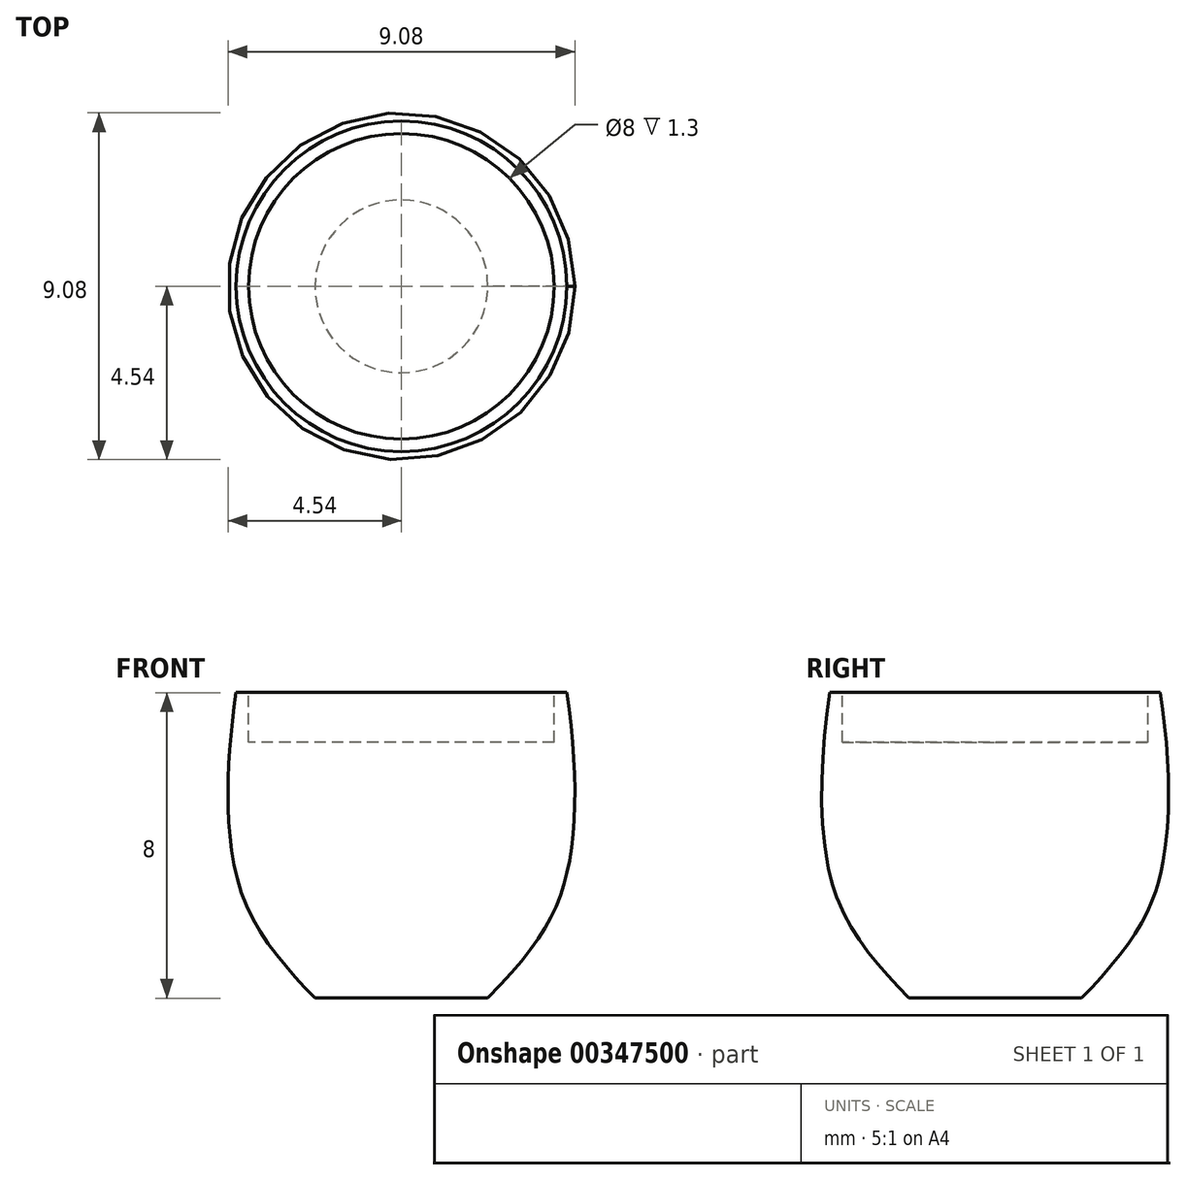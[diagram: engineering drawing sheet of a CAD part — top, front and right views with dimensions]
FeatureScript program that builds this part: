
annotation { "Feature Type Name" : "Feature", "Feature Type Description" : "" }
export const myFeature = defineFeature(function(context is Context, id is Id, definition is map)
    precondition{}
    {
        {
            var Q0;
            Q0=qCreatedBy(makeId("Front.planeOp"),FACE);
            var sketch = newSketch(context, id + "F0", { "sketchPlane" : qUnion([Q0])});
            skLineSegment(sketch, "E0", {"start": v(0, 18.23) * mm, "end": v(4.33, 18.23) * mm});
            skFitSpline(sketch, "E1", {"points": [v(4.33, 18.23) * mm, v(4.33, 13.48) * mm, v(2.26, 10.23) * mm], "startDerivative": vector(1.51, -10.18) * mm, "endDerivative": vector(-7.9, -8.2) * mm});
            skLineSegment(sketch, "E2", {"start": v(2.26, 10.23) * mm, "end": v(0, 10.23) * mm});
            skLineSegment(sketch, "E3", {"start": v(0, 18.23) * mm, "end": v(0, 10.23) * mm});
            skSolve(sketch);
        }
        {
            var Q0;
            Q0=makeQuery(id+"F0.imprint","IMPRINT",FACE,{"disambiguationData":[TD([[makeQuery(id+"F0.imprint","IMPRINT",EDGE,{"derivedFrom":sQuery(id+"F0.wireOp",EDGE,"E0")}),-1.0]])]});
            var Q1;
            Q1=sQuery(id+"F0.wireOp",EDGE,"E3");
            revolve(context, id + "F1", {"entities" : qUnion([Q0]), "axis" : qUnion([Q1]), "revolveType" : RevolveType.FULL});
        }
        {
            var Q0;
            Q0=makeQuery(id+"F1.opRevolve","SWEPT_FACE",FACE,{"disambiguationData":[OSD([sQuery(id+"F0.wireOp",EDGE,"E0")])]});
            var sketch = newSketch(context, id + "F2", { "sketchPlane" : qUnion([Q0])});
            skCircle(sketch, "E4", {"center": v(0, 0) * mm, "radius": 4 * mm});
            skSolve(sketch);
        }
        {
            var Q0;
            Q0=makeQuery(id+"F2.imprint","IMPRINT",FACE,{"disambiguationData":[TD([[makeQuery(id+"F2.imprint","IMPRINT",EDGE,{"derivedFrom":sQuery(id+"F2.wireOp",EDGE,"E4")}),1.0]])]});
            extrude(context, id + "F3", {"entities" : qUnion([Q0]), "operationType" : NewBodyOperationType.REMOVE, "oppositeDirection" : true, "depth" : 1.3 * mm});
        }
    });
